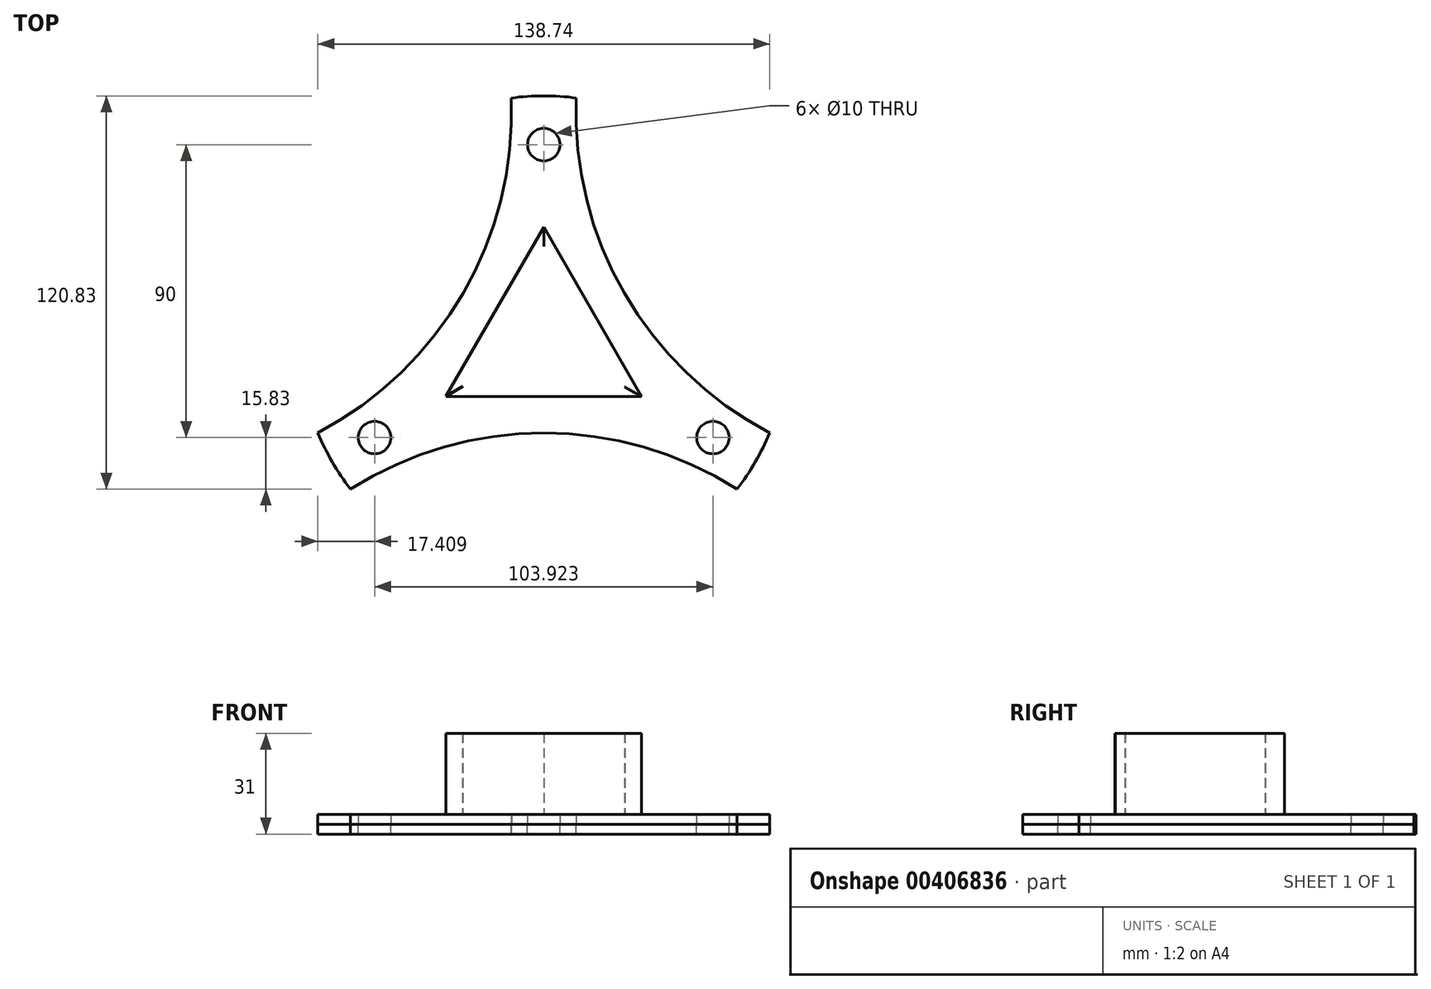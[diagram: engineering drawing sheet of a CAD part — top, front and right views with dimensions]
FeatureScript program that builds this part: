
annotation { "Feature Type Name" : "Feature", "Feature Type Description" : "" }
export const myFeature = defineFeature(function(context is Context, id is Id, definition is map)
    precondition{}
    {
        {
            var Q0;
            Q0=qCreatedBy(makeId("Top.planeOp"),FACE);
            var sketch = newSketch(context, id + "F0", { "sketchPlane" : qUnion([Q0])});
            skLineSegment(sketch, "E0", {"start": v(0, 0) * mm, "end": v(0, 75) * mm});
            skLineSegment(sketch, "E1.1.1", {"start": v(0, 0) * mm, "end": v(-64.95, -37.5) * mm});
            skLineSegment(sketch, "E1.2.1", {"start": v(0, 0) * mm, "end": v(64.95, -37.5) * mm});
            skPoint(sketch, "E1.center", {"position": v(0, 0) * mm});
            skArc(sketch, "E2", {"start": v(-69.37, -28.5) * mm, "mid": v(-24.78, 14.3) * mm, "end": v(-10, 74.33) * mm});
            skArc(sketch, "E3.1.0", {"start": v(59.37, -45.83) * mm, "mid": v(0, -28.61) * mm, "end": v(-59.37, -45.83) * mm});
            skArc(sketch, "E3.2.0", {"start": v(10, 74.33) * mm, "mid": v(24.78, 14.3) * mm, "end": v(69.37, -28.5) * mm});
            skCircle(sketch, "E4", {"center": v(0, 60) * mm, "radius": 5 * mm});
            skCircle(sketch, "E5.1.0", {"center": v(-51.96, -30) * mm, "radius": 5 * mm});
            skCircle(sketch, "E5.2.0", {"center": v(51.96, -30) * mm, "radius": 5 * mm});
            skArc(sketch, "E6", {"start": v(-10, 74.33) * mm, "mid": v(0, 75) * mm, "end": v(10, 74.33) * mm});
            skArc(sketch, "E7", {"start": v(69.37, -28.5) * mm, "mid": v(64.95, -37.5) * mm, "end": v(59.37, -45.83) * mm});
            skArc(sketch, "E8", {"start": v(-59.37, -45.83) * mm, "mid": v(-64.95, -37.5) * mm, "end": v(-69.37, -28.5) * mm});
            skSolve(sketch);
        }
        {
            var Q0;
            {var subQ0=sQuery(id+"F0.wireOp",EDGE,"E5.1.0");var subQ1=sQuery(id+"F0.wireOp",EDGE,"E1.1.1");var subQ2=makeQuery(id+"F0.imprint","INTERSECT",VERTEX,{"disambiguationData":[OD(0.0)],"derivedFrom":[subQ1,subQ0]});Q0=makeQuery(id+"F0.imprint","IMPRINT",FACE,{"disambiguationData":[TD([[makeQuery(id+"F0.imprint","IMPRINT",EDGE,{"disambiguationData":[TD([[subQ2,-1.0]])],"derivedFrom":subQ1}),1.0]])]});}
            var Q1;
            {var subQ0=sQuery(id+"F0.wireOp",EDGE,"E5.1.0");var subQ1=sQuery(id+"F0.wireOp",EDGE,"E1.1.1");var subQ2=makeQuery(id+"F0.imprint","INTERSECT",VERTEX,{"disambiguationData":[OD(0.0)],"derivedFrom":[subQ1,subQ0]});Q1=makeQuery(id+"F0.imprint","IMPRINT",FACE,{"disambiguationData":[TD([[makeQuery(id+"F0.imprint","IMPRINT",EDGE,{"disambiguationData":[TD([[subQ2,-1.0]])],"derivedFrom":subQ1}),-1.0]])]});}
            var Q2;
            {var subQ0=sQuery(id+"F0.wireOp",EDGE,"E5.2.0");var subQ1=sQuery(id+"F0.wireOp",EDGE,"E1.2.1");var subQ2=makeQuery(id+"F0.imprint","INTERSECT",VERTEX,{"disambiguationData":[OD(0.0)],"derivedFrom":[subQ1,subQ0]});Q2=makeQuery(id+"F0.imprint","IMPRINT",FACE,{"disambiguationData":[TD([[makeQuery(id+"F0.imprint","IMPRINT",EDGE,{"disambiguationData":[TD([[subQ2,-1.0]])],"derivedFrom":subQ1}),-1.0]])]});}
            var Q3;
            {var subQ0=sQuery(id+"F0.wireOp",EDGE,"E5.2.0");var subQ1=sQuery(id+"F0.wireOp",EDGE,"E1.2.1");var subQ2=makeQuery(id+"F0.imprint","INTERSECT",VERTEX,{"disambiguationData":[OD(0.0)],"derivedFrom":[subQ1,subQ0]});Q3=makeQuery(id+"F0.imprint","IMPRINT",FACE,{"disambiguationData":[TD([[makeQuery(id+"F0.imprint","IMPRINT",EDGE,{"disambiguationData":[TD([[subQ2,-1.0]])],"derivedFrom":subQ1}),1.0]])]});}
            var Q4;
            {var subQ0=sQuery(id+"F0.wireOp",EDGE,"E4");var subQ1=sQuery(id+"F0.wireOp",EDGE,"E0");var subQ2=makeQuery(id+"F0.imprint","INTERSECT",VERTEX,{"disambiguationData":[OD(0.0)],"derivedFrom":[subQ1,subQ0]});Q4=makeQuery(id+"F0.imprint","IMPRINT",FACE,{"disambiguationData":[TD([[makeQuery(id+"F0.imprint","IMPRINT",EDGE,{"disambiguationData":[TD([[subQ2,-1.0]])],"derivedFrom":subQ1}),1.0]])]});}
            var Q5;
            {var subQ0=sQuery(id+"F0.wireOp",EDGE,"E4");var subQ1=sQuery(id+"F0.wireOp",EDGE,"E0");var subQ2=makeQuery(id+"F0.imprint","INTERSECT",VERTEX,{"disambiguationData":[OD(0.0)],"derivedFrom":[subQ1,subQ0]});Q5=makeQuery(id+"F0.imprint","IMPRINT",FACE,{"disambiguationData":[TD([[makeQuery(id+"F0.imprint","IMPRINT",EDGE,{"disambiguationData":[TD([[subQ2,-1.0]])],"derivedFrom":subQ1}),-1.0]])]});}
            extrude(context, id + "F1", {"entities" : qUnion([Q0, Q1, Q2, Q3, Q4, Q5]), "oppositeDirection" : true, "depth" : 3 * mm});
        }
        {
            var Q0;
            {var subQ0=sQuery(id+"F0.wireOp",EDGE,"E5.1.0");var subQ1=sQuery(id+"F0.wireOp",EDGE,"E1.1.1");var subQ2=makeQuery(id+"F0.imprint","INTERSECT",VERTEX,{"disambiguationData":[OD(0.0)],"derivedFrom":[subQ1,subQ0]});Q0=makeQuery(id+"F0.imprint","IMPRINT",FACE,{"disambiguationData":[TD([[makeQuery(id+"F0.imprint","IMPRINT",EDGE,{"disambiguationData":[TD([[subQ2,-1.0]])],"derivedFrom":subQ1}),-1.0]])]});}
            var Q1;
            {var subQ0=sQuery(id+"F0.wireOp",EDGE,"E5.1.0");var subQ1=sQuery(id+"F0.wireOp",EDGE,"E1.1.1");var subQ2=makeQuery(id+"F0.imprint","INTERSECT",VERTEX,{"disambiguationData":[OD(0.0)],"derivedFrom":[subQ1,subQ0]});Q1=makeQuery(id+"F0.imprint","IMPRINT",FACE,{"disambiguationData":[TD([[makeQuery(id+"F0.imprint","IMPRINT",EDGE,{"disambiguationData":[TD([[subQ2,-1.0]])],"derivedFrom":subQ1}),1.0]])]});}
            var Q2;
            {var subQ0=sQuery(id+"F0.wireOp",EDGE,"E4");var subQ1=sQuery(id+"F0.wireOp",EDGE,"E0");var subQ2=makeQuery(id+"F0.imprint","INTERSECT",VERTEX,{"disambiguationData":[OD(0.0)],"derivedFrom":[subQ1,subQ0]});Q2=makeQuery(id+"F0.imprint","IMPRINT",FACE,{"disambiguationData":[TD([[makeQuery(id+"F0.imprint","IMPRINT",EDGE,{"disambiguationData":[TD([[subQ2,-1.0]])],"derivedFrom":subQ1}),-1.0]])]});}
            var Q3;
            {var subQ0=sQuery(id+"F0.wireOp",EDGE,"E4");var subQ1=sQuery(id+"F0.wireOp",EDGE,"E0");var subQ2=makeQuery(id+"F0.imprint","INTERSECT",VERTEX,{"disambiguationData":[OD(0.0)],"derivedFrom":[subQ1,subQ0]});Q3=makeQuery(id+"F0.imprint","IMPRINT",FACE,{"disambiguationData":[TD([[makeQuery(id+"F0.imprint","IMPRINT",EDGE,{"disambiguationData":[TD([[subQ2,-1.0]])],"derivedFrom":subQ1}),1.0]])]});}
            var Q4;
            {var subQ0=sQuery(id+"F0.wireOp",EDGE,"E5.2.0");var subQ1=sQuery(id+"F0.wireOp",EDGE,"E1.2.1");var subQ2=makeQuery(id+"F0.imprint","INTERSECT",VERTEX,{"disambiguationData":[OD(0.0)],"derivedFrom":[subQ1,subQ0]});Q4=makeQuery(id+"F0.imprint","IMPRINT",FACE,{"disambiguationData":[TD([[makeQuery(id+"F0.imprint","IMPRINT",EDGE,{"disambiguationData":[TD([[subQ2,-1.0]])],"derivedFrom":subQ1}),1.0]])]});}
            var Q5;
            {var subQ0=sQuery(id+"F0.wireOp",EDGE,"E5.2.0");var subQ1=sQuery(id+"F0.wireOp",EDGE,"E1.2.1");var subQ2=makeQuery(id+"F0.imprint","INTERSECT",VERTEX,{"disambiguationData":[OD(0.0)],"derivedFrom":[subQ1,subQ0]});Q5=makeQuery(id+"F0.imprint","IMPRINT",FACE,{"disambiguationData":[TD([[makeQuery(id+"F0.imprint","IMPRINT",EDGE,{"disambiguationData":[TD([[subQ2,-1.0]])],"derivedFrom":subQ1}),-1.0]])]});}
            var Q6;
            {var subQ13=sQuery(id+"F0.wireOp",EDGE,"E3.1.0");Q6=makeQuery(id+"F0.imprint","IMPRINT",FACE,{"disambiguationData":[TD([[makeQuery(id+"F0.imprint","IMPRINT",EDGE,{"derivedFrom":subQ13}),-1.0]])]});}
            var Q7;
            {var subQ8=sQuery(id+"F0.wireOp",EDGE,"E3.2.0");Q7=makeQuery(id+"F0.imprint","IMPRINT",FACE,{"disambiguationData":[TD([[makeQuery(id+"F0.imprint","IMPRINT",EDGE,{"derivedFrom":subQ8}),-1.0]])]});}
            var Q8;
            {var subQ13=sQuery(id+"F0.wireOp",EDGE,"E2");Q8=makeQuery(id+"F0.imprint","IMPRINT",FACE,{"disambiguationData":[TD([[makeQuery(id+"F0.imprint","IMPRINT",EDGE,{"derivedFrom":subQ13}),-1.0]])]});}
            extrude(context, id + "F2", {"entities" : qUnion([Q0, Q1, Q2, Q3, Q4, Q5, Q6, Q7, Q8]), "depth" : 3 * mm});
        }
        {
            var Q0;
            Q0=makeQuery(id+"F2.opExtrude","CAP_FACE",FACE,{"disambiguationData":[OSD([sQuery(id+"F0.wireOp",EDGE,"E2"),sQuery(id+"F0.wireOp",EDGE,"E3.1.0"),sQuery(id+"F0.wireOp",EDGE,"E3.2.0"),sQuery(id+"F0.wireOp",EDGE,"E6"),sQuery(id+"F0.wireOp",EDGE,"E7"),sQuery(id+"F0.wireOp",EDGE,"E8")])],"isStart":false});
            var sketch = newSketch(context, id + "F3", { "sketchPlane" : qUnion([Q0])});
            skPoint(sketch, "E9.center", {"position": v(-0.05, 0.03) * mm});
            skLineSegment(sketch, "E10", {"start": v(0, 34.67) * mm, "end": v(-30.08, -17.25) * mm});
            skPoint(sketch, "E11.center", {"position": v(0, 0) * mm});
            skLineSegment(sketch, "E12", {"start": v(0.04, 28.76) * mm, "end": v(0, 28.69) * mm});
            skLineSegment(sketch, "E13.trimOffspring", {"start": v(-24.87, -14.24) * mm, "end": v(-24.93, -14.34) * mm});
            skLineSegment(sketch, "E14", {"start": v(-24.87, -14.24) * mm, "end": v(0, 28.69) * mm});
            skLineSegment(sketch, "E15", {"start": v(0.04, 28.76) * mm, "end": v(0, 34.67) * mm});
            skLineSegment(sketch, "E16", {"start": v(-24.87, -14.24) * mm, "end": v(-30.08, -17.25) * mm});
            skLineSegment(sketch, "E17.1.0", {"start": v(24.77, -14.41) * mm, "end": v(29.97, -17.42) * mm});
            skLineSegment(sketch, "E17.1.2", {"start": v(-24.93, -14.34) * mm, "end": v(-30.03, -17.34) * mm});
            skLineSegment(sketch, "E17.1.4", {"start": v(24.77, -14.41) * mm, "end": v(-24.84, -14.34) * mm});
            skPoint(sketch, "E17.1.5", {"position": v(0, -0.06) * mm});
            skLineSegment(sketch, "E17.1.6", {"start": v(24.77, -14.41) * mm, "end": v(24.88, -14.41) * mm});
            skLineSegment(sketch, "E17.1.7", {"start": v(-24.93, -14.34) * mm, "end": v(-24.84, -14.34) * mm});
            skLineSegment(sketch, "E17.1.8", {"start": v(-30.03, -17.34) * mm, "end": v(29.97, -17.42) * mm});
            skLineSegment(sketch, "E17.2.0", {"start": v(0.1, 28.65) * mm, "end": v(0.1, 34.67) * mm});
            skLineSegment(sketch, "E17.2.2", {"start": v(24.88, -14.41) * mm, "end": v(30.03, -17.34) * mm});
            skLineSegment(sketch, "E17.2.4", {"start": v(0.1, 28.65) * mm, "end": v(24.84, -14.34) * mm});
            skPoint(sketch, "E17.2.5", {"position": v(0.05, 0.03) * mm});
            skLineSegment(sketch, "E17.2.6", {"start": v(0.1, 28.65) * mm, "end": v(0.04, 28.76) * mm});
            skLineSegment(sketch, "E17.2.7", {"start": v(24.88, -14.41) * mm, "end": v(24.84, -14.34) * mm});
            skLineSegment(sketch, "E17.2.8", {"start": v(30.03, -17.34) * mm, "end": v(0.1, 34.67) * mm});
            skSolve(sketch);
        }
        {
            var Q0;
            Q0 = qSketchRegion(id + "F3", true);
            extrude(context, id + "F4", {"entities" : qUnion([Q0]), "operationType" : NewBodyOperationType.ADD, "depth" : 25 * mm, "offsetDistance" : 25 * mm});
        }
    });
